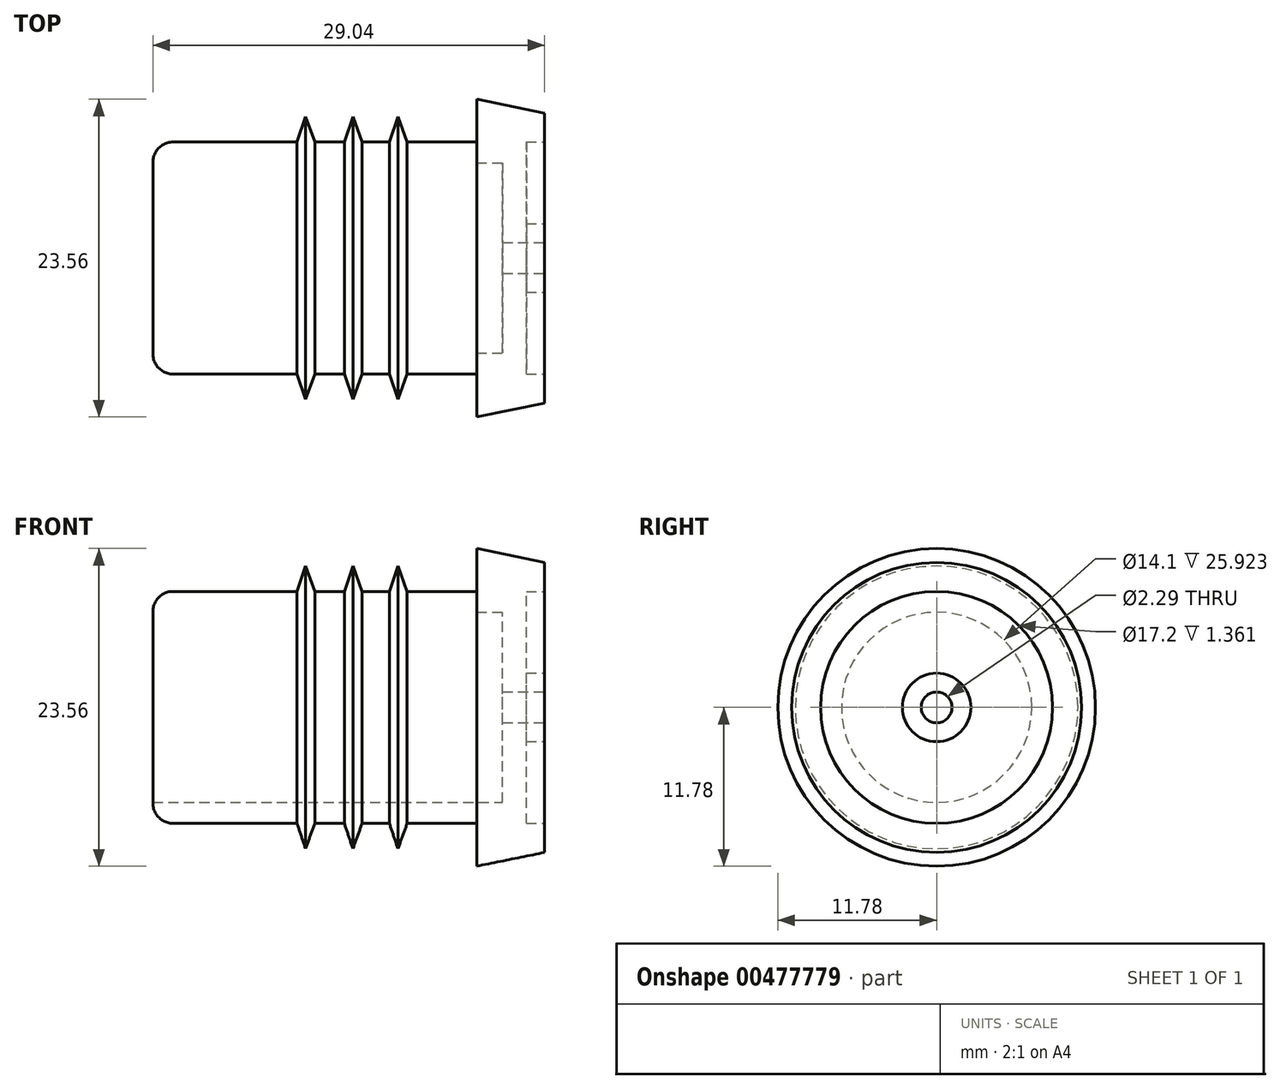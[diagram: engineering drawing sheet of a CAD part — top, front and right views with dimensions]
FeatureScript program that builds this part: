
annotation { "Feature Type Name" : "Feature", "Feature Type Description" : "" }
export const myFeature = defineFeature(function(context is Context, id is Id, definition is map)
    precondition{}
    {
        {
            var Q0;
            Q0=qCreatedBy(makeId("Front.planeOp"),FACE);
            var sketch = newSketch(context, id + "F0", { "sketchPlane" : qUnion([Q0])});
            skLineSegment(sketch, "E0", {"start": v(0, 0) * mm, "end": v(-24, 0) * mm});
            skLineSegment(sketch, "E1", {"start": v(-24, 8.6) * mm, "end": v(0, 8.6) * mm});
            skLineSegment(sketch, "E2", {"start": v(0, 11.78) * mm, "end": v(5.04, 10.75) * mm});
            skLineSegment(sketch, "E3", {"start": v(5.04, 0) * mm, "end": v(0, 0) * mm});
            skLineSegment(sketch, "E4", {"start": v(-13.31, 8.6) * mm, "end": v(-12.68, 10.48) * mm});
            skLineSegment(sketch, "E5", {"start": v(-12.68, 10.48) * mm, "end": v(-12, 8.6) * mm});
            skLineSegment(sketch, "E6", {"start": v(-9.8, 8.6) * mm, "end": v(-9.17, 10.48) * mm});
            skLineSegment(sketch, "E7", {"start": v(-9.17, 10.48) * mm, "end": v(-8.5, 8.6) * mm});
            skLineSegment(sketch, "E8", {"start": v(-6.47, 8.6) * mm, "end": v(-5.83, 10.48) * mm});
            skLineSegment(sketch, "E9", {"start": v(-5.83, 10.48) * mm, "end": v(-5.15, 8.6) * mm});
            skPoint(sketch, "E10", {"position": v(5.04, 0) * mm});
            skLineSegment(sketch, "E11", {"start": v(5.04, 10.75) * mm, "end": v(5.04, 8.6) * mm});
            skLineSegment(sketch, "E12", {"start": v(5.04, 8.6) * mm, "end": v(3.68, 8.6) * mm});
            skLineSegment(sketch, "E13", {"start": v(3.68, 8.6) * mm, "end": v(3.68, 2.54) * mm});
            skLineSegment(sketch, "E14", {"start": v(3.68, 2.54) * mm, "end": v(5.04, 2.54) * mm});
            skLineSegment(sketch, "E15", {"start": v(5.04, 2.54) * mm, "end": v(5.04, 1.14) * mm});
            skLineSegment(sketch, "E16", {"start": v(5.04, 1.14) * mm, "end": v(1.92, 1.14) * mm});
            skLineSegment(sketch, "E17", {"start": v(0, 11.78) * mm, "end": v(0, 8.6) * mm});
            skLineSegment(sketch, "E18", {"start": v(-24, 8.6) * mm, "end": v(-24, 7.05) * mm});
            skLineSegment(sketch, "E19", {"start": v(1.92, 1.14) * mm, "end": v(1.92, 7.05) * mm});
            skLineSegment(sketch, "E20", {"start": v(1.92, 7.05) * mm, "end": v(-24, 7.05) * mm});
            skSolve(sketch);
        }
        {
            var Q0;
            {var subQ0=sQuery(id+"F0.wireOp",EDGE,"E6");Q0=makeQuery(id+"F0.imprint","IMPRINT",FACE,{"disambiguationData":[TD([[makeQuery(id+"F0.imprint","IMPRINT",EDGE,{"derivedFrom":subQ0}),-1.0]])]});}
            var Q1;
            {var subQ0=sQuery(id+"F0.wireOp",EDGE,"E8");Q1=makeQuery(id+"F0.imprint","IMPRINT",FACE,{"disambiguationData":[TD([[makeQuery(id+"F0.imprint","IMPRINT",EDGE,{"derivedFrom":subQ0}),-1.0]])]});}
            var Q2;
            Q2=makeQuery(id+"F0.imprint","IMPRINT",FACE,{"disambiguationData":[TD([[makeQuery(id+"F0.imprint","IMPRINT",EDGE,{"derivedFrom":sQuery(id+"F0.wireOp",EDGE,"E2")}),-1.0]])]});
            var Q3;
            {var subQ0=sQuery(id+"F0.wireOp",EDGE,"E4");Q3=makeQuery(id+"F0.imprint","IMPRINT",FACE,{"disambiguationData":[TD([[makeQuery(id+"F0.imprint","IMPRINT",EDGE,{"derivedFrom":subQ0}),-1.0]])]});}
            var Q4;
            Q4=sQuery(id+"F0.wireOp",EDGE,"E0");
            revolve(context, id + "F1", {"entities" : qUnion([Q0, Q1, Q2, Q3]), "axis" : qUnion([Q4]), "revolveType" : RevolveType.FULL});
        }
        {
            var Q0;
            Q0=makeQuery(id+"F1.opRevolve","SWEPT_EDGE",EDGE,{"disambiguationData":[OSD([sQuery(id+"F0.wireOp",EDGE,"E1"),sQuery(id+"F0.wireOp",EDGE,"E18")])]});
            fillet(context, id + "F2", {"entities" : qUnion([Q0]), "radius" : 1.5 * mm, "tangentPropagation" : true, "allowEdgeOverflow" : false});
        }
    });
